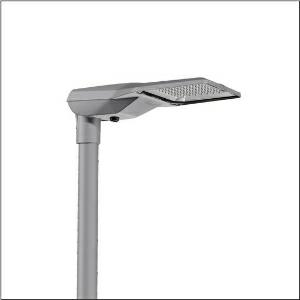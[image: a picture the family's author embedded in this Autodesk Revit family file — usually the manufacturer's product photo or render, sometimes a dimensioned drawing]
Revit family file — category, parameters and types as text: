
# Revit family: streetlight_sl_21_midi___st1_0a_5xe3d33r08mb_0fe4
name_source: partatom
category: Lighting Fixtures
units: mm (PartAtom-declared; Revit-internal decimal feet)

## family parameters
Cut with Voids When Loaded = No
Host = Face
Light Source = No
Part Type = Normal
Room Calculation Point = No
Round Connector Dimension = Use Diameter
Shared = No

## types (1)
- --- (1 x LED, 18270 lm, 136 W, 3000K)
    Apparent Load = 136 VA
    CIE Flux Codes = 37 72 97 100 100
    Color Rendering = 70
    Color Temperature = 3000K
    Default Elevation = 1800 mm
    Description = Streetlight SL 21 midi, mast luminaire, primary light control with lens, of PMMA, primary optical cover: cover, of toughened safety glass, transparent, light distribution: ST1.0a, light emission: direct distribution, primary light characteristic: asymmetric, installation type: side-entry, post-top, LED, High Power LED, rated luminous flux: 18.270lm, luminous efficacy: 134lm/W, light colour: 730, colour temperature: 3000K, control gear: D4i, control: flexible luminous flux parameterisation, time-dependent luminous flux control, constant luminous flux control, overheat protection, pre-setting: logarithmic dimming characteristic, mains connection: 230..240V, AC, 50/60Hz, start of lifetime: 136W, end of service life: 142W, reduction: 61W, luminaire housing, of diecast aluminium, powder-coated, Siteco® metallic grey (DB 702S), corrosivity category C5 mid according to DIN EN ISO 12944, please order mast flange separately, inclination adjustable: 0°, 5°, 10°, 15°, sealing non-destructively replaceable, multi-level sealing system, length: 644mm, width: 335mm, height: 110mm, mast flange for spigot size: 42mm (side-entry): 5XC10008XM4, 60/48mm (side-entry/post-top): 5XC10108XM2, 76/60mm (side-entry/post-top): 5XC10108XM1, mounting height: 4..8m, Smart Interface below, protection rating (complete): IP66, insulation class (complete): insulation class II (safety insulation), certification: CE, ENEC, ENEC+, VDE, impact resistance: IK10, permissible operating ambient temperature for outdoor applications: -40..+50°C, standard-compliant lighting for roads and squares, packaging unit: 1 piece

Light Distribution: ST1.0a
    Height = 111 mm
    Lamp = 1 x LED
    Lamp Light Flux = 18270 lm
    Lamp Power = 136 W
    Lamp count = 1
    Length = 644 mm
    Luminous efficacy = 134 lm/W
    Manufacturer = Siteco
    ModVariant = No
    Model = 5XE3D33R08MB
    Number of Poles = 1
    OnlyDefault = Yes
    Power Factor = 1
    Product Name = Streetlight SL 21 midi | ST1.0a
    Product group = mast luminaire | pylon top
    ProductGroupID = 6100
    Protection Class = Protection class II
    Protection Degree = IP 66
    RLX_Detail_Level = 1
    RLX_Emergency_Light_Flux = 0 lm
    RLX_Emergency_Type = 0
    RLX_Emergency_Type_DB = No
    RlxData = <blob elided: 26929 chars, md5=a1078209>
    Socket = socket
    Standby Power = 0 W
    System Light Flux = 18270 lm
    System Power = 136 W
    Type Comments = factory setting: luminous flux: 100 % | dim-lin: 254 | 695 mA
    Type Image = l_1004300.jpg
    URL = http://relux.com
    VarID = @adj_210681
    Voltage = 0 V
    Weight = 0.00 kg
    Width = 336 mm

## geometry (parser evidence)
native form markers: Blend x4, Sweep x13
no freeform markers — native parametric forms only
